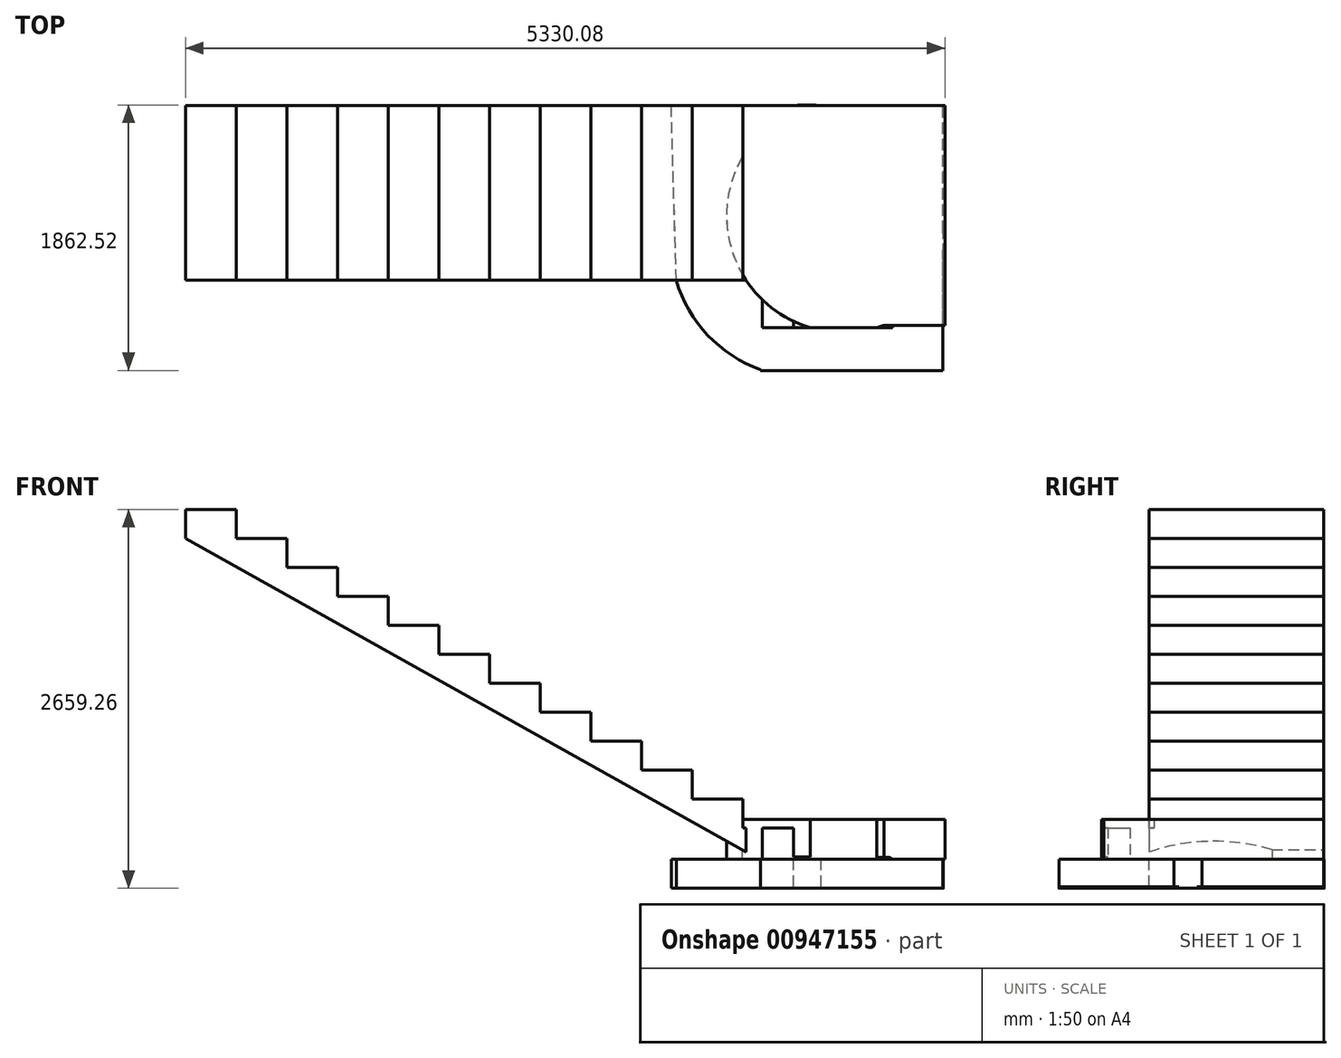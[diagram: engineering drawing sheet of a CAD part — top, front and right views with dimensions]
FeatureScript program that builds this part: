
annotation { "Feature Type Name" : "Feature", "Feature Type Description" : "" }
export const myFeature = defineFeature(function(context is Context, id is Id, definition is map)
    precondition{}
    {
        {
            var Q0;
            Q0=qCreatedBy(makeId("Front.planeOp"),FACE);
            var sketch = newSketch(context, id + "F0", { "sketchPlane" : qUnion([Q0])});
            skLineSegment(sketch, "E0", {"start": v(0, 0) * mm, "end": v(0, 2921) * mm});
            skLineSegment(sketch, "E1", {"start": v(0, 0) * mm, "end": v(5334, 0) * mm});
            skLineSegment(sketch, "E2", {"start": v(5334, 0) * mm, "end": v(0, 2921) * mm});
            skSolve(sketch);
        }
        {
            var Q0;
            Q0 = qSketchRegion(id + "F0", true);
            extrude(context, id + "F1", {"entities" : qUnion([Q0]), "depth" : 3810 * mm, "offsetDistance" : 25.4 * mm});
        }
        {
            var Q0;
            Q0=makeQuery(id+"F1.opExtrude","SWEPT_FACE",FACE,{"disambiguationData":[OSD([sQuery(id+"F0.wireOp",EDGE,"E2")])]});
            fillet(context, id + "F2", {"entities" : qUnion([Q0]), "radius" : 5.08 * mm, "tangentPropagation" : true, "allowEdgeOverflow" : false});
        }
        {
            var Q0;
            Q0=makeQuery(id+"F1.opExtrude","CAP_FACE",FACE,{"disambiguationData":[OSD([sQuery(id+"F0.wireOp",EDGE,"E0"),sQuery(id+"F0.wireOp",EDGE,"E1"),sQuery(id+"F0.wireOp",EDGE,"E2")])],"isStart":false});
            var sketch = newSketch(context, id + "F3", { "sketchPlane" : qUnion([Q0])});
            skLineSegment(sketch, "E3", {"start": v(0, 0) * mm, "end": v(3665.59, 0) * mm});
            skLineSegment(sketch, "E4", {"start": v(3665.59, 0) * mm, "end": v(3665.59, 907.86) * mm});
            skLineSegment(sketch, "E5", {"start": v(3665.59, 907.86) * mm, "end": v(0.62, 2914.87) * mm});
            skLineSegment(sketch, "E6", {"start": v(0.62, 2914.87) * mm, "end": v(0, 0) * mm});
            skSolve(sketch);
        }
        {
            var Q0;
            Q0=makeQuery(id+"F1.opExtrude","SWEPT_FACE",FACE,{"disambiguationData":[OSD([sQuery(id+"F0.wireOp",EDGE,"E1")])]});
            var sketch = newSketch(context, id + "F4", { "sketchPlane" : qUnion([Q0])});
            skLineSegment(sketch, "E7", {"start": v(0, 3810) * mm, "end": v(0, 1224.28) * mm});
            skLineSegment(sketch, "E8", {"start": v(0, 1224.28) * mm, "end": v(4046.59, 1224.28) * mm});
            skLineSegment(sketch, "E9", {"start": v(4046.59, 3810) * mm, "end": v(0, 3810) * mm});
            skLineSegment(sketch, "E10", {"start": v(4046.59, 1224.28) * mm, "end": v(4046.59, 3810) * mm});
            skSolve(sketch);
        }
        {
            var Q0;
            Q0 = qSketchRegion(id + "F4", true);
            extrude(context, id + "F5", {"entities" : qUnion([Q0]), "operationType" : NewBodyOperationType.REMOVE, "oppositeDirection" : true, "depth" : 3454.4 * mm, "offsetDistance" : 25.4 * mm});
        }
        {
            var Q0;
            Q0=makeQuery(id+"F3.imprint","IMPRINT",FACE,{"disambiguationData":[TD([[makeQuery(id+"F3.imprint","IMPRINT",EDGE,{"derivedFrom":sQuery(id+"F3.wireOp",EDGE,"E3")}),1.0]])]});
            var sketch = newSketch(context, id + "F6", { "sketchPlane" : qUnion([Q0])});
            skLineSegment(sketch, "E11", {"start": v(355.6, 2659.26) * mm, "end": v(0, 2659.26) * mm});
            skLineSegment(sketch, "E12", {"start": v(355.6, 2659.26) * mm, "end": v(355.6, 2456.06) * mm});
            skLineSegment(sketch, "E13", {"start": v(355.6, 2456.06) * mm, "end": v(711.2, 2456.06) * mm});
            skLineSegment(sketch, "E14", {"start": v(711.2, 2456.06) * mm, "end": v(711.2, 2252.86) * mm});
            skLineSegment(sketch, "E15", {"start": v(711.2, 2252.86) * mm, "end": v(1066.8, 2252.86) * mm});
            skLineSegment(sketch, "E16", {"start": v(1066.8, 2252.86) * mm, "end": v(1066.8, 2049.66) * mm});
            skLineSegment(sketch, "E17", {"start": v(1066.8, 2049.66) * mm, "end": v(1422.4, 2049.66) * mm});
            skLineSegment(sketch, "E18", {"start": v(1422.4, 2049.66) * mm, "end": v(1422.4, 1846.46) * mm});
            skLineSegment(sketch, "E19", {"start": v(1422.4, 1846.46) * mm, "end": v(1778, 1846.46) * mm});
            skLineSegment(sketch, "E20", {"start": v(1778, 1846.46) * mm, "end": v(1778, 1643.26) * mm});
            skLineSegment(sketch, "E21", {"start": v(1778, 1643.26) * mm, "end": v(2133.6, 1643.26) * mm});
            skLineSegment(sketch, "E22", {"start": v(2133.6, 1643.26) * mm, "end": v(2133.6, 1440.06) * mm});
            skLineSegment(sketch, "E23", {"start": v(2133.6, 1440.06) * mm, "end": v(2489.2, 1440.06) * mm});
            skLineSegment(sketch, "E24", {"start": v(2489.2, 1440.06) * mm, "end": v(2489.2, 1236.86) * mm});
            skLineSegment(sketch, "E25", {"start": v(2489.2, 1236.86) * mm, "end": v(2844.8, 1236.86) * mm});
            skLineSegment(sketch, "E26", {"start": v(2844.8, 1236.86) * mm, "end": v(2844.8, 1033.66) * mm});
            skLineSegment(sketch, "E27", {"start": v(2844.8, 1033.66) * mm, "end": v(3200.4, 1033.66) * mm});
            skLineSegment(sketch, "E28", {"start": v(3200.4, 1033.66) * mm, "end": v(3200.4, 830.46) * mm});
            skLineSegment(sketch, "E29", {"start": v(3200.4, 830.46) * mm, "end": v(3556, 830.46) * mm});
            skLineSegment(sketch, "E30", {"start": v(3556, 830.46) * mm, "end": v(3556, 627.26) * mm});
            skLineSegment(sketch, "E31", {"start": v(3556, 627.26) * mm, "end": v(3911.6, 627.26) * mm});
            skLineSegment(sketch, "E32", {"start": v(3911.6, 627.26) * mm, "end": v(3911.6, 424.06) * mm});
            skLineSegment(sketch, "E33", {"start": v(3911.6, 424.06) * mm, "end": v(4267.2, 424.06) * mm});
            skLineSegment(sketch, "E34", {"start": v(4267.2, 424.06) * mm, "end": v(4267.2, 220.86) * mm});
            skLineSegment(sketch, "E35", {"start": v(4267.2, 220.86) * mm, "end": v(4622.8, 220.86) * mm});
            skLineSegment(sketch, "E36", {"start": v(4622.8, 220.86) * mm, "end": v(4622.8, 17.66) * mm});
            skLineSegment(sketch, "E37", {"start": v(0, 2659.26) * mm, "end": v(0, 2456.06) * mm});
            skLineSegment(sketch, "E38", {"start": v(0, 2456.06) * mm, "end": v(4419.6, 17.66) * mm});
            skLineSegment(sketch, "E39", {"start": v(4622.8, 17.66) * mm, "end": v(4419.6, 17.66) * mm});
            skLineSegment(sketch, "E40", {"start": v(2852.36, 882.35) * mm, "end": v(2856.96, 1525.92) * mm});
            skLineSegment(sketch, "E41", {"start": v(2856.96, 1525.92) * mm, "end": v(5320.9, 166.5) * mm});
            skLineSegment(sketch, "E42", {"start": v(5320.9, 166.5) * mm, "end": v(5315.98, 0) * mm});
            skLineSegment(sketch, "E43", {"start": v(5315.98, 0) * mm, "end": v(0, 0) * mm});
            skLineSegment(sketch, "E44", {"start": v(0, 0) * mm, "end": v(0, 2659.26) * mm});
            skLineSegment(sketch, "E45", {"start": v(0, 3038.56) * mm, "end": v(2856.96, 1525.92) * mm});
            skPoint(sketch, "E46.end.orphan", {"position": v(2846.18, 17.66) * mm});
            skLineSegment(sketch, "E47", {"start": v(2852.36, 882.35) * mm, "end": v(2846.18, 0) * mm});
            skLineSegment(sketch, "E48.top", {"start": v(5320.9, -137.84) * mm, "end": v(-325.42, -137.84) * mm});
            skLineSegment(sketch, "E48.left", {"start": v(5320.9, 166.5) * mm, "end": v(5320.9, -137.84) * mm});
            skLineSegment(sketch, "E48.right", {"start": v(-325.42, 166.5) * mm, "end": v(-325.42, -137.84) * mm});
            skLineSegment(sketch, "E49", {"start": v(-325.42, 166.5) * mm, "end": v(-325.42, 3048.74) * mm});
            skLineSegment(sketch, "E50", {"start": v(-325.42, 3048.74) * mm, "end": v(0, 3038.56) * mm});
            skLineSegment(sketch, "E51", {"start": v(4622.8, 17.66) * mm, "end": v(5320.9, 17.66) * mm});
            skLineSegment(sketch, "E52", {"start": v(4958.14, 215.33) * mm, "end": v(4622.8, 220.86) * mm});
            skLineSegment(sketch, "E53", {"start": v(4958.14, 215.33) * mm, "end": v(5320.9, 17.66) * mm});
            skSolve(sketch);
        }
        {
            var Q0;
            {var subQ5=sQuery(id+"F6.wireOp",EDGE,"E42");var subQ14=sQuery(id+"F6.wireOp",EDGE,"E37");var subQ20=sQuery(id+"F6.wireOp",EDGE,"E51");var subQ21=makeQuery(id+"F6.imprint","INTERSECT",VERTEX,{"derivedFrom":[subQ5,subQ20]});var subQ23=sQuery(id+"F6.wireOp",EDGE,"E53");var subQ28=makeQuery(id+"F6.imprint","INTERSECT",VERTEX,{"derivedFrom":[subQ5,subQ23]});var subQ29=makeQuery(id+"F6.imprint","IMPRINT",EDGE,{"disambiguationData":[TD([[subQ28,1.0]])],"derivedFrom":subQ5});var subQ31=sQuery(id+"F6.wireOp",EDGE,"E32");var subQ38=sQuery(id+"F6.wireOp",EDGE,"E28");var subQ42=sQuery(id+"F6.wireOp",EDGE,"E12");Q0=qUnion([makeQuery(id+"F6.imprint","IMPRINT",FACE,{"disambiguationData":[TD([[subQ29,1.0]])]}),makeQuery(id+"F6.imprint","IMPRINT",FACE,{"disambiguationData":[TD([[makeQuery(id+"F6.imprint","IMPRINT",EDGE,{"disambiguationData":[TD([[subQ21,1.0]])],"derivedFrom":subQ5}),1.0]])]}),makeQuery(id+"F6.imprint","IMPRINT",FACE,{"disambiguationData":[TD([[makeQuery(id+"F6.imprint","IMPRINT",EDGE,{"derivedFrom":subQ42}),1.0]])]}),makeQuery(id+"F6.imprint","IMPRINT",FACE,{"disambiguationData":[TD([[makeQuery(id+"F6.imprint","IMPRINT",EDGE,{"derivedFrom":subQ38}),1.0]])]}),makeQuery(id+"F6.imprint","IMPRINT",FACE,{"disambiguationData":[TD([[makeQuery(id+"F6.imprint","IMPRINT",EDGE,{"derivedFrom":subQ31}),1.0]])]}),makeQuery(id+"F6.imprint","IMPRINT",FACE,{"disambiguationData":[TD([[makeQuery(id+"F6.imprint","IMPRINT",EDGE,{"derivedFrom":subQ14}),-1.0]])]})]);}
            extrude(context, id + "F7", {"entities" : qUnion([Q0]), "operationType" : NewBodyOperationType.REMOVE, "oppositeDirection" : true, "depth" : 4292.6 * mm, "offsetDistance" : 25.4 * mm});
        }
        {
            var Q0;
            Q0=makeQuery(id+"F1.opExtrude","CAP_FACE",FACE,{"disambiguationData":[OSD([sQuery(id+"F0.wireOp",EDGE,"E0"),sQuery(id+"F0.wireOp",EDGE,"E1"),sQuery(id+"F0.wireOp",EDGE,"E2")])],"isStart":true});
            var sketch = newSketch(context, id + "F8", { "sketchPlane" : qUnion([Q0])});
            skLineSegment(sketch, "E54", {"start": v(0, 0) * mm, "end": v(0, 2456.06) * mm});
            skLineSegment(sketch, "E55", {"start": v(0, 2456.06) * mm, "end": v(-4386.64, 0) * mm});
            skLineSegment(sketch, "E56", {"start": v(-4386.64, 0) * mm, "end": v(0, 0) * mm});
            skSolve(sketch);
        }
        {
            var Q0;
            Q0 = qSketchRegion(id + "F8", true);
            extrude(context, id + "F9", {"entities" : qUnion([Q0]), "operationType" : NewBodyOperationType.REMOVE, "oppositeDirection" : true, "depth" : 5537.2 * mm, "offsetDistance" : 25.4 * mm});
        }
        {
            var Q0;
            Q0=qCreatedBy(makeId("Top.planeOp"),FACE);
            var sketch = newSketch(context, id + "F10", { "sketchPlane" : qUnion([Q0])});
            skLineSegment(sketch, "E57.bottom", {"start": v(5313.46, 0) * mm, "end": v(3408.46, 0) * mm});
            skLineSegment(sketch, "E57.top", {"start": v(5313.46, -1905) * mm, "end": v(4034.4, -1905) * mm});
            skLineSegment(sketch, "E57.left", {"start": v(5313.46, 0) * mm, "end": v(5313.46, -1905) * mm});
            skLineSegment(sketch, "E58", {"start": v(3408.46, -1905) * mm, "end": v(5313.46, 0) * mm, "construction": true});
            skLineSegment(sketch, "E59", {"start": v(5313.46, -1905) * mm, "end": v(3408.46, 0) * mm, "construction": true});
            skArc(sketch, "E60", {"start": v(4458.46, 0) * mm, "mid": v(4360.96, 4.98) * mm, "end": v(4263.47, 0) * mm});
            skArc(sketch, "E61.trimOffspring", {"start": v(3443.8, -1227.37) * mm, "mid": v(3829.2, -1748.74) * mm, "end": v(4458.46, -1905) * mm});
            skLineSegment(sketch, "E62.bottom", {"start": v(3408.46, -1227.37) * mm, "end": v(4034.4, -1227.37) * mm});
            skLineSegment(sketch, "E62.right", {"start": v(4034.4, -1227.37) * mm, "end": v(4034.4, -1905) * mm});
            skArc(sketch, "E63.trimOffspring", {"start": v(5313.46, -1050) * mm, "mid": v(5318.44, -952.5) * mm, "end": v(5313.46, -855) * mm});
            skLineSegment(sketch, "E64", {"start": v(3443.8, -1227.37) * mm, "end": v(3408.46, 0) * mm});
            skSolve(sketch);
        }
        {
            var Q0;
            Q0 = qSketchRegion(id + "F10", true);
            extrude(context, id + "F11", {"entities" : qUnion([Q0]), "operationType" : NewBodyOperationType.ADD, "depth" : 203.2 * mm, "offsetDistance" : 25.4 * mm});
        }
        {
            var Q0;
            Q0=qCreatedBy(makeId("Top.planeOp"),FACE);
            var sketch = newSketch(context, id + "F12", { "sketchPlane" : qUnion([Q0])});
            skLineSegment(sketch, "E65.bottom", {"start": v(3984.5, -1857.54) * mm, "end": v(5445.54, -1857.54) * mm});
            skLineSegment(sketch, "E65.top", {"start": v(3984.5, -3945.85) * mm, "end": v(5445.54, -3945.85) * mm});
            skLineSegment(sketch, "E65.left", {"start": v(3984.5, -1857.54) * mm, "end": v(3984.5, -3945.85) * mm});
            skLineSegment(sketch, "E65.right", {"start": v(5445.54, -1857.54) * mm, "end": v(5445.54, -3945.85) * mm});
            skSolve(sketch);
        }
        {
            var Q0;
            Q0 = qSketchRegion(id + "F12", true);
            extrude(context, id + "F13", {"entities" : qUnion([Q0]), "operationType" : NewBodyOperationType.REMOVE, "depth" : 1066.8 * mm, "offsetDistance" : 25.4 * mm});
        }
        {
            var Q0;
            {var subQ0=sQuery(id+"F10.wireOp",EDGE,"E57.left");var subQ1=sQuery(id+"F10.wireOp",EDGE,"E57.bottom");var subQ2=sQuery(id+"F10.wireOp",EDGE,"E60");var subQ3=sQuery(id+"F10.wireOp",EDGE,"E62.right");var subQ4=sQuery(id+"F10.wireOp",EDGE,"E64");var subQ5=sQuery(id+"F10.wireOp",EDGE,"E57.top");var subQ6=sQuery(id+"F10.wireOp",EDGE,"E61.trimOffspring");Q0=makeQuery(id+"F11.boolean.opBoolean","SPLIT",FACE,{"disambiguationData":[TD([makeQuery(id+"F5.boolean.opBoolean","COPY",FACE,{"derivedFrom":makeQuery(id+"F5.opExtrude","SWEPT_FACE",FACE,{"disambiguationData":[OSD([sQuery(id+"F4.wireOp",EDGE,"E8")])]})})])],"derivedFrom":makeQuery(id+"F11.opExtrude","CAP_FACE",FACE,{"disambiguationData":[OSD([subQ1,subQ5,subQ0,subQ2,subQ6,subQ3,sQuery(id+"F10.wireOp",EDGE,"E63.trimOffspring"),subQ4])],"isStart":false})});}
            var sketch = newSketch(context, id + "F14", { "sketchPlane" : qUnion([Q0])});
            skPoint(sketch, "E66.oppositeSnap0", {"position": v(4046.59, -1540.91) * mm});
            skLineSegment(sketch, "E66.bottom", {"start": v(5330.08, 0) * mm, "end": v(3905.97, 0) * mm});
            skLineSegment(sketch, "E66.top", {"start": v(5330.08, -1540.91) * mm, "end": v(4901.3, -1540.91) * mm});
            skLineSegment(sketch, "E66.left", {"start": v(5330.08, 0) * mm, "end": v(5330.08, -1540.91) * mm});
            skLineSegment(sketch, "E66.right", {"start": v(3905.97, 0) * mm, "end": v(3905.97, -1178.9) * mm});
            skLineSegment(sketch, "E67", {"start": v(5330.08, 0) * mm, "end": v(3905.97, -1540.91) * mm, "construction": true});
            skLineSegment(sketch, "E68", {"start": v(5330.08, -1540.91) * mm, "end": v(5108.76, -1227.37) * mm, "construction": true});
            skLineSegment(sketch, "E69", {"start": v(3905.97, 0) * mm, "end": v(5330.08, -1540.91) * mm, "construction": true});
            skArc(sketch, "E70", {"start": v(4334.74, 0) * mm, "mid": v(3847.57, -1053.74) * mm, "end": v(4901.3, -1540.91) * mm});
            skArc(sketch, "E71.trimOffspring", {"start": v(5330.08, -362) * mm, "mid": v(5147.58, -143.23) * mm, "end": v(4901.3, 0) * mm});
            skArc(sketch, "E72.trimOffspring", {"start": v(5175.18, -1373.3) * mm, "mid": v(5186.18, -1362.94) * mm, "end": v(5197, -1352.38) * mm});
            skLineSegment(sketch, "E73", {"start": v(4334.74, 0) * mm, "end": v(4901.3, 0) * mm});
            skLineSegment(sketch, "E74", {"start": v(5330.08, -362) * mm, "end": v(5330.08, -1540.91) * mm});
            skSolve(sketch);
        }
        {
            var Q0;
            {var subQ6=sQuery(id+"F14.wireOp",EDGE,"E70");var subQ7=sQuery(id+"F14.wireOp",EDGE,"E66.right");var subQ8=makeQuery(id+"F14.imprint","INTERSECT",VERTEX,{"disambiguationData":[OD(0.0)],"derivedFrom":[subQ7,subQ6]});var subQ10=makeQuery(id+"F14.imprint","IMPRINT",EDGE,{"disambiguationData":[TD([[subQ8,-1.0]])],"derivedFrom":subQ7});var subQ18=sQuery(id+"F14.wireOp",EDGE,"E66.bottom");var subQ19=makeQuery(id+"F14.imprint","INTERSECT",VERTEX,{"derivedFrom":[subQ18,subQ6]});var subQ21=sQuery(id+"F14.wireOp",EDGE,"E66.top");var subQ23=sQuery(id+"F14.wireOp",EDGE,"E71.trimOffspring");var subQ26=makeQuery(id+"F14.imprint","IMPRINT",EDGE,{"derivedFrom":subQ23});Q0=qUnion([makeQuery(id+"F14.imprint","IMPRINT",FACE,{"disambiguationData":[TD([[subQ26,-1.0]])]}),makeQuery(id+"F14.imprint","IMPRINT",FACE,{"disambiguationData":[TD([[subQ10,-1.0]])]}),makeQuery(id+"F14.imprint","IMPRINT",FACE,{"disambiguationData":[TD([[makeQuery(id+"F14.imprint","IMPRINT",EDGE,{"disambiguationData":[TD([[subQ19,-1.0]])],"derivedFrom":subQ18}),1.0]])]}),makeQuery(id+"F14.imprint","IMPRINT",FACE,{"disambiguationData":[TD([[makeQuery(id+"F14.imprint","IMPRINT",EDGE,{"disambiguationData":[TD([[subQ8,1.0]])],"derivedFrom":subQ7}),1.0]])]}),makeQuery(id+"F14.imprint","IMPRINT",FACE,{"disambiguationData":[TD([[makeQuery(id+"F14.imprint","IMPRINT",EDGE,{"derivedFrom":subQ21}),-1.0]])]}),makeQuery(id+"F14.imprint","IMPRINT",FACE,{"disambiguationData":[TD([[subQ10,1.0]])]})]);}
            extrude(context, id + "F15", {"entities" : qUnion([Q0]), "operationType" : NewBodyOperationType.ADD, "depth" : 279.4 * mm, "offsetDistance" : 25.4 * mm});
        }
        {
            var Q0;
            Q0=makeQuery(id+"F15.opExtrude","SWEPT_FACE",FACE,{"disambiguationData":[OSD([sQuery(id+"F14.wireOp",EDGE,"E66.left")])]});
            var sketch = newSketch(context, id + "F16", { "sketchPlane" : qUnion([Q0])});
            skLineSegment(sketch, "E75.bottom", {"start": v(-1557.16, 514.12) * mm, "end": v(-1979.75, 514.12) * mm});
            skLineSegment(sketch, "E75.top", {"start": v(-1557.16, 203.2) * mm, "end": v(-1979.75, 203.2) * mm});
            skLineSegment(sketch, "E75.left", {"start": v(-1557.16, 514.12) * mm, "end": v(-1557.16, 203.2) * mm});
            skLineSegment(sketch, "E75.right", {"start": v(-1979.75, 514.12) * mm, "end": v(-1979.75, 203.2) * mm});
            skSolve(sketch);
        }
        {
            var Q0;
            Q0 = qSketchRegion(id + "F16", true);
            extrude(context, id + "F17", {"entities" : qUnion([Q0]), "operationType" : NewBodyOperationType.REMOVE, "oppositeDirection" : true, "depth" : 3728.72 * mm, "offsetDistance" : 25.4 * mm});
        }
    });
